# Revit family: ledbalance-p_14w-dim-830_840_850_523003012900_2cc8
name_source: partatom
category: Lighting Fixtures
units: mm (PartAtom-declared; Revit-internal decimal feet)

## family parameters
Cut with Voids When Loaded = No
Host = Face
Light Source = No
Part Type = Normal
Room Calculation Point = No
Round Connector Dimension = Use Diameter
Shared = No

## types (1)
- LEDBalance-P 14W-DIM-830/840/850 (1 x LED, 840 lm, 4000)
    Apparent Load = 14 VA
    Approval mark = CE
    CIE Flux Codes = 40 78 96 100 100
    Color Rendering = 80
    Color Temperature = 4000
    Control Gear = Electronic ballast
    Default Elevation = 1800 mm
    Description = Desk Lamp Balance 14W-840lm-3/4/5000K-
    Frequency = 60 Hz
    Height = 570 mm
    Lamp = 1 x LED
    Lamp Light Flux = 840 lm
    Lamp count = 1
    Length = 440 mm
    Luminous efficacy = 60 lm/W
    Manufacturer = OPPLE
    ModVariant = No
    Model = 523003012900
    Mounting Place = Table
    Mounting Type = Freestanding
    Number of Poles = 1
    OnlyDefault = Yes
    Power Factor = 1
    Product Name = LEDBalance-P 14W-DIM-830/840/850
    Product group = Desk luminaire
    ProductGroupID = 21
    Protection Class = Protection class II
    Protection Degree = IP 20
    RLX_Detail_Level = 1
    RLX_Emergency_Light_Flux = 0 lm
    RLX_Emergency_Type = 0
    RLX_Emergency_Type_DB = No
    RlxData = <blob elided: 246029 chars, md5=1bdeb5da>
    Socket = socket
    Standby Power = 0 W
    System Light Flux = 843 lm
    System Power = 14 W
    Type Comments = Product without accessories
    Type Image = web_balance.jpg
    URL = http://relux.com
    VarID = ---
    Voltage = 230 V
    Voltage Range = 220-240 V
    Weight = 0.00 kg
    Width = 196 mm

## geometry (parser evidence)
native form markers: Sweep x15
no freeform markers — native parametric forms only
